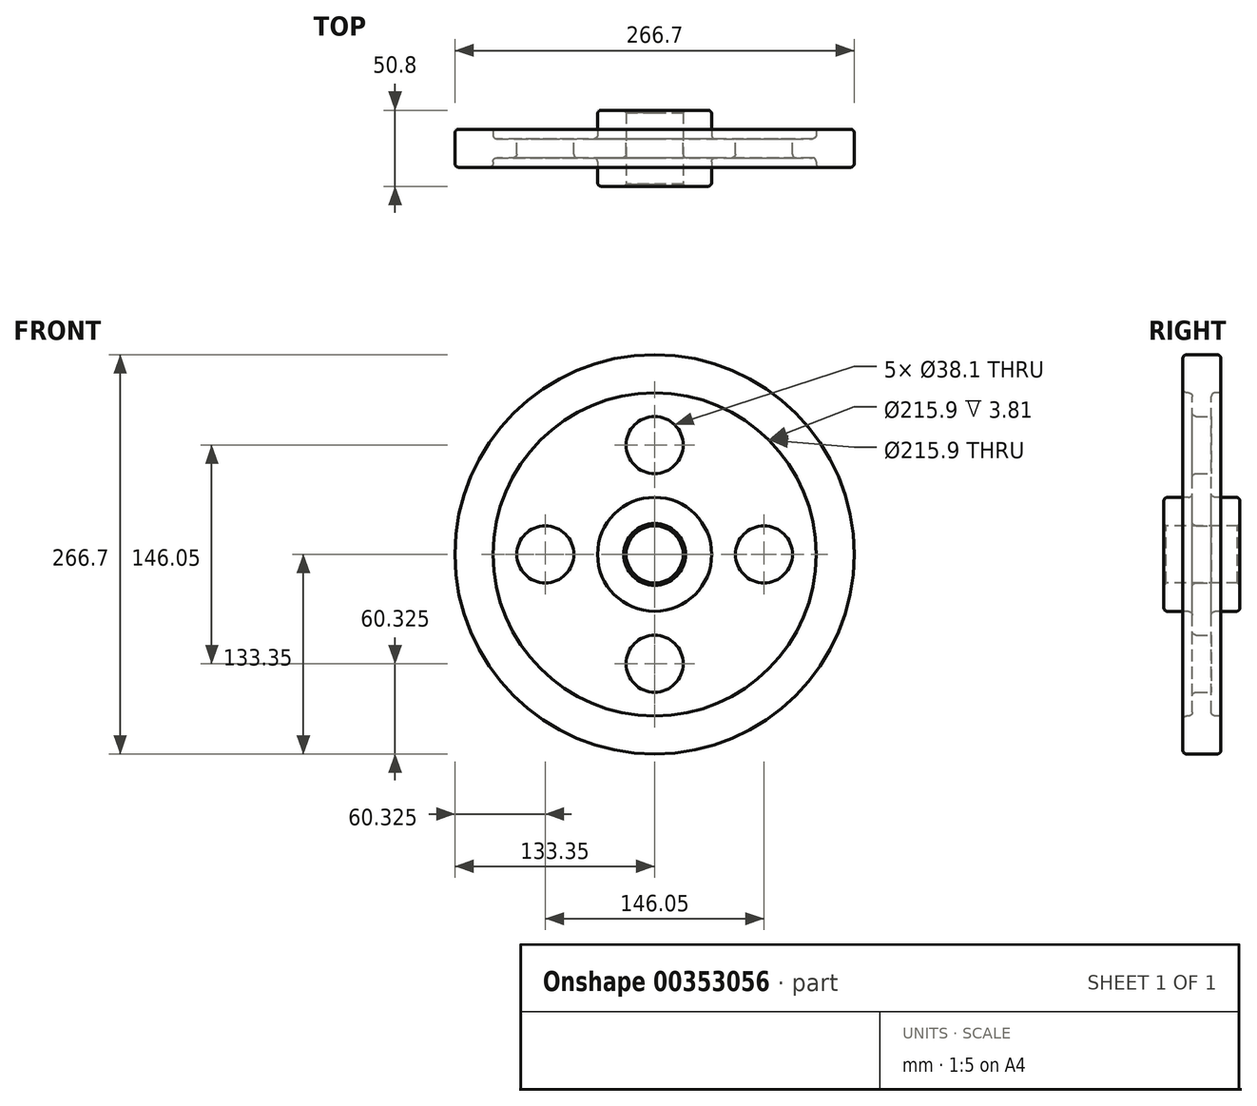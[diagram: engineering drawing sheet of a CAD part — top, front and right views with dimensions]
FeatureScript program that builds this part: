
annotation { "Feature Type Name" : "Feature", "Feature Type Description" : "" }
export const myFeature = defineFeature(function(context is Context, id is Id, definition is map)
    precondition{}
    {
        {
            var Q0;
            Q0=qCreatedBy(makeId("Right.planeOp"),FACE);
            var sketch = newSketch(context, id + "F0", { "sketchPlane" : qUnion([Q0])});
            skLineSegment(sketch, "E0", {"start": v(0, 0) * mm, "end": v(76.24, 0) * mm, "construction": true});
            skLineSegment(sketch, "E1.0", {"start": v(6.35, 38.1) * mm, "end": v(25.4, 38.1) * mm});
            skLineSegment(sketch, "E2.0", {"start": v(6.35, 107.95) * mm, "end": v(12.7, 107.95) * mm});
            skLineSegment(sketch, "E3.0", {"start": v(25.4, 19.05) * mm, "end": v(25.4, 38.1) * mm});
            skLineSegment(sketch, "E4.trimOffspring", {"start": v(6.35, 38.1) * mm, "end": v(6.35, 107.95) * mm});
            skLineSegment(sketch, "E5.trimOffspring", {"start": v(12.7, 107.95) * mm, "end": v(12.7, 133.35) * mm});
            skLineSegment(sketch, "E6.MirrorCS", {"start": v(-12.7, 107.95) * mm, "end": v(-12.7, 133.35) * mm});
            skLineSegment(sketch, "E7.MirrorCS", {"start": v(-6.35, 107.95) * mm, "end": v(-12.7, 107.95) * mm});
            skLineSegment(sketch, "E8.MirrorCS", {"start": v(-6.35, 38.1) * mm, "end": v(-6.35, 107.95) * mm});
            skLineSegment(sketch, "E9.MirrorCS", {"start": v(-6.35, 38.1) * mm, "end": v(-25.4, 38.1) * mm});
            skLineSegment(sketch, "E10.MirrorCS", {"start": v(-25.4, 19.05) * mm, "end": v(-25.4, 38.1) * mm});
            skLineSegment(sketch, "E11", {"start": v(-25.4, 19.05) * mm, "end": v(25.4, 19.05) * mm});
            skLineSegment(sketch, "E12", {"start": v(-12.7, 133.35) * mm, "end": v(12.7, 133.35) * mm});
            skSolve(sketch);
        }
        {
            var Q0;
            Q0=makeQuery(id+"F0.imprint","IMPRINT",FACE,{"disambiguationData":[TD([[makeQuery(id+"F0.imprint","IMPRINT",EDGE,{"derivedFrom":sQuery(id+"F0.wireOp",EDGE,"E1.0")}),-1.0]])]});
            var Q1;
            Q1=sQuery(id+"F0.wireOp",EDGE,"E0");
            revolve(context, id + "F1", {"entities" : qUnion([Q0]), "axis" : qUnion([Q1]), "revolveType" : RevolveType.FULL});
        }
        {
            var Q0;
            Q0=makeQuery(id+"F1.opRevolve","SWEPT_FACE",FACE,{"disambiguationData":[OSD([sQuery(id+"F0.wireOp",EDGE,"E4.trimOffspring")])]});
            var sketch = newSketch(context, id + "F2", { "sketchPlane" : qUnion([Q0])});
            skLineSegment(sketch, "E13", {"start": v(0, 0) * mm, "end": v(0, 73.03) * mm});
            skCircle(sketch, "E14", {"center": v(0, 73.03) * mm, "radius": 19.05 * mm});
            skCircle(sketch, "E15.1.0", {"center": v(-73.03, 0) * mm, "radius": 19.05 * mm});
            skCircle(sketch, "E15.2.0", {"center": v(0, -73.03) * mm, "radius": 19.05 * mm});
            skCircle(sketch, "E15.3.0", {"center": v(73.03, 0) * mm, "radius": 19.05 * mm});
            skPoint(sketch, "E15.center", {"position": v(0, 0) * mm});
            skSolve(sketch);
        }
        {
            var Q0;
            Q0=makeQuery(id+"F2.imprint","IMPRINT",FACE,{"disambiguationData":[TD([[makeQuery(id+"F2.imprint","IMPRINT",EDGE,{"derivedFrom":sQuery(id+"F2.wireOp",EDGE,"E15.1.0")}),1.0]])]});
            var Q1;
            Q1=makeQuery(id+"F2.imprint","IMPRINT",FACE,{"disambiguationData":[TD([[makeQuery(id+"F2.imprint","IMPRINT",EDGE,{"derivedFrom":sQuery(id+"F2.wireOp",EDGE,"E15.2.0")}),1.0]])]});
            var Q2;
            Q2=makeQuery(id+"F2.imprint","IMPRINT",FACE,{"disambiguationData":[TD([[makeQuery(id+"F2.imprint","IMPRINT",EDGE,{"derivedFrom":sQuery(id+"F2.wireOp",EDGE,"E15.3.0")}),1.0]])]});
            var Q3;
            Q3=makeQuery(id+"F2.imprint","IMPRINT",FACE,{"disambiguationData":[TD([[makeQuery(id+"F2.imprint","IMPRINT",EDGE,{"derivedFrom":sQuery(id+"F2.wireOp",EDGE,"E14")}),1.0]])]});
            extrude(context, id + "F3", {"entities" : qUnion([Q0, Q1, Q2, Q3]), "operationType" : NewBodyOperationType.REMOVE, "oppositeDirection" : true, "depth" : 25.4 * mm});
        }
        {
            var Q0;
            Q0=makeQuery(id+"F3.boolean.opBoolean","COPY",EDGE,{"derivedFrom":makeQuery(id+"F3.opExtrude","CAP_EDGE",EDGE,{"disambiguationData":[OSD([sQuery(id+"F2.wireOp",EDGE,"E15.2.0")])],"isStart":true})});
            var Q1;
            Q1=makeQuery(id+"F3.boolean.opBoolean","COPY",EDGE,{"derivedFrom":makeQuery(id+"F3.opExtrude","CAP_EDGE",EDGE,{"disambiguationData":[OSD([sQuery(id+"F2.wireOp",EDGE,"E15.1.0")])],"isStart":true})});
            var Q2;
            Q2=makeQuery(id+"F3.boolean.opBoolean","COPY",EDGE,{"derivedFrom":makeQuery(id+"F3.opExtrude","CAP_EDGE",EDGE,{"disambiguationData":[OSD([sQuery(id+"F2.wireOp",EDGE,"E14")])],"isStart":true})});
            var Q3;
            Q3=makeQuery(id+"F3.boolean.opBoolean","COPY",EDGE,{"derivedFrom":makeQuery(id+"F3.opExtrude","CAP_EDGE",EDGE,{"disambiguationData":[OSD([sQuery(id+"F2.wireOp",EDGE,"E15.3.0")])],"isStart":true})});
            var Q4;
            Q4=makeQuery(id+"F1.opRevolve","SWEPT_EDGE",EDGE,{"disambiguationData":[OSD([sQuery(id+"F0.wireOp",EDGE,"E2.0"),sQuery(id+"F0.wireOp",EDGE,"E4.trimOffspring")])]});
            var Q5;
            Q5=makeQuery(id+"F1.opRevolve","SWEPT_EDGE",EDGE,{"disambiguationData":[OSD([sQuery(id+"F0.wireOp",EDGE,"E5.trimOffspring"),sQuery(id+"F0.wireOp",EDGE,"E12")])]});
            var Q6;
            Q6=makeQuery(id+"F1.opRevolve","SWEPT_EDGE",EDGE,{"disambiguationData":[OSD([sQuery(id+"F0.wireOp",EDGE,"E1.0"),sQuery(id+"F0.wireOp",EDGE,"E4.trimOffspring")])]});
            var Q7;
            Q7=makeQuery(id+"F1.opRevolve","SWEPT_EDGE",EDGE,{"disambiguationData":[OSD([sQuery(id+"F0.wireOp",EDGE,"E8.MirrorCS"),sQuery(id+"F0.wireOp",EDGE,"E9.MirrorCS")])]});
            var Q8;
            Q8=makeQuery(id+"F3.boolean.opBoolean","INTERSECT",EDGE,{"derivedFrom":[makeQuery(id+"F1.opRevolve","SWEPT_FACE",FACE,{"disambiguationData":[OSD([sQuery(id+"F0.wireOp",EDGE,"E8.MirrorCS")])]}),makeQuery(id+"F3.opExtrude","SWEPT_FACE",FACE,{"disambiguationData":[OSD([sQuery(id+"F2.wireOp",EDGE,"E14")])]})]});
            var Q9;
            Q9=makeQuery(id+"F3.boolean.opBoolean","INTERSECT",EDGE,{"derivedFrom":[makeQuery(id+"F1.opRevolve","SWEPT_FACE",FACE,{"disambiguationData":[OSD([sQuery(id+"F0.wireOp",EDGE,"E8.MirrorCS")])]}),makeQuery(id+"F3.opExtrude","SWEPT_FACE",FACE,{"disambiguationData":[OSD([sQuery(id+"F2.wireOp",EDGE,"E15.3.0")])]})]});
            var Q10;
            Q10=makeQuery(id+"F3.boolean.opBoolean","INTERSECT",EDGE,{"derivedFrom":[makeQuery(id+"F1.opRevolve","SWEPT_FACE",FACE,{"disambiguationData":[OSD([sQuery(id+"F0.wireOp",EDGE,"E8.MirrorCS")])]}),makeQuery(id+"F3.opExtrude","SWEPT_FACE",FACE,{"disambiguationData":[OSD([sQuery(id+"F2.wireOp",EDGE,"E15.1.0")])]})]});
            var Q11;
            Q11=makeQuery(id+"F3.boolean.opBoolean","INTERSECT",EDGE,{"derivedFrom":[makeQuery(id+"F1.opRevolve","SWEPT_FACE",FACE,{"disambiguationData":[OSD([sQuery(id+"F0.wireOp",EDGE,"E8.MirrorCS")])]}),makeQuery(id+"F3.opExtrude","SWEPT_FACE",FACE,{"disambiguationData":[OSD([sQuery(id+"F2.wireOp",EDGE,"E15.2.0")])]})]});
            var Q12;
            Q12=makeQuery(id+"F1.opRevolve","SWEPT_EDGE",EDGE,{"disambiguationData":[OSD([sQuery(id+"F0.wireOp",EDGE,"E7.MirrorCS"),sQuery(id+"F0.wireOp",EDGE,"E8.MirrorCS")])]});
            var Q13;
            Q13=makeQuery(id+"F1.opRevolve","SWEPT_EDGE",EDGE,{"disambiguationData":[OSD([sQuery(id+"F0.wireOp",EDGE,"E9.MirrorCS"),sQuery(id+"F0.wireOp",EDGE,"E10.MirrorCS")])]});
            var Q14;
            Q14=makeQuery(id+"F1.opRevolve","SWEPT_EDGE",EDGE,{"disambiguationData":[OSD([sQuery(id+"F0.wireOp",EDGE,"E1.0"),sQuery(id+"F0.wireOp",EDGE,"E3.0")])]});
            var Q15;
            Q15=makeQuery(id+"F1.opRevolve","SWEPT_EDGE",EDGE,{"disambiguationData":[OSD([sQuery(id+"F0.wireOp",EDGE,"E6.MirrorCS"),sQuery(id+"F0.wireOp",EDGE,"E12")])]});
            var Q16;
            Q16=makeQuery(id+"F1.opRevolve","SWEPT_EDGE",EDGE,{"disambiguationData":[OSD([sQuery(id+"F0.wireOp",EDGE,"E6.MirrorCS"),sQuery(id+"F0.wireOp",EDGE,"E7.MirrorCS")])]});
            fillet(context, id + "F4", {"entities" : qUnion([Q0, Q1, Q2, Q3, Q4, Q5, Q6, Q7, Q8, Q9, Q10, Q11, Q12, Q13, Q14, Q15, Q16]), "radius" : 2.54 * mm, "tangentPropagation" : true, "allowEdgeOverflow" : false});
        }
        {
            var Q0;
            Q0=makeQuery(id+"F1.opRevolve","SWEPT_FACE",FACE,{"disambiguationData":[OSD([sQuery(id+"F0.wireOp",EDGE,"E11")])]});
            chamfer(context, id + "F5", {"entities" : qUnion([Q0]), "width" : 1.59 * mm, "tangentPropagation" : true});
        }
    });
